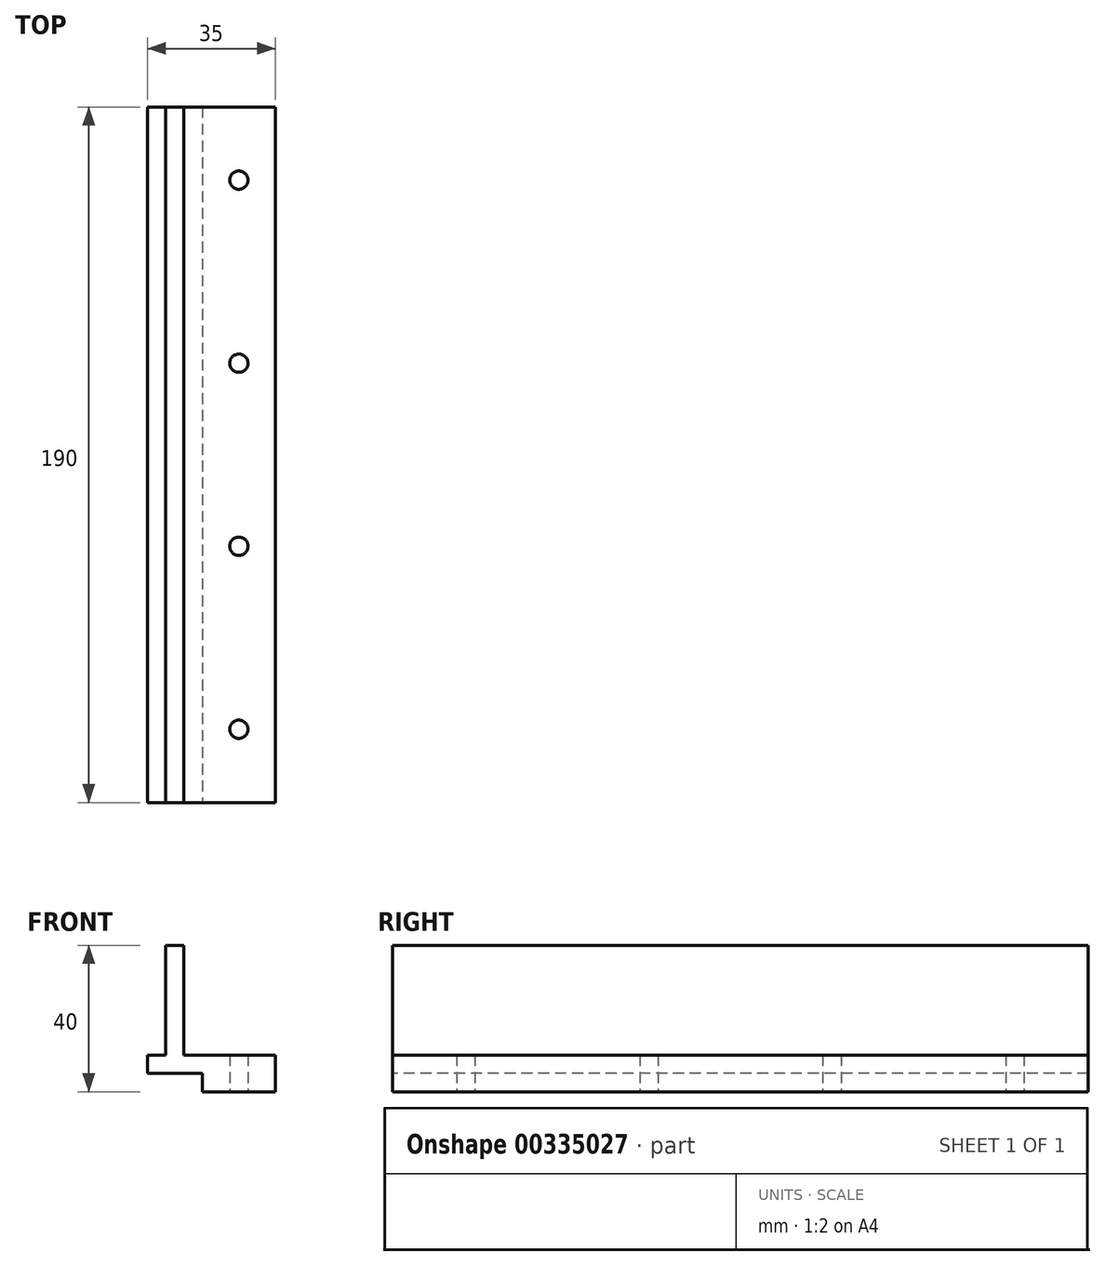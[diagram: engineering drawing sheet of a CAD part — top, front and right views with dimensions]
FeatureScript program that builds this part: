
annotation { "Feature Type Name" : "Feature", "Feature Type Description" : "" }
export const myFeature = defineFeature(function(context is Context, id is Id, definition is map)
    precondition{}
    {
        {
            var Q0;
            Q0=qCreatedBy(makeId("Top.planeOp"),FACE);
            var sketch = newSketch(context, id + "F0", { "sketchPlane" : qUnion([Q0])});
            skLineSegment(sketch, "E0", {"start": v(0, 35.83) * mm, "end": v(0, -48.01) * mm, "construction": true});
            skCircle(sketch, "E1", {"center": v(0, -28.01) * mm, "radius": 2.5 * mm});
            skCircle(sketch, "E2.0.1.0", {"center": v(0, 21.99) * mm, "radius": 2.5 * mm});
            skCircle(sketch, "E2.0.2.0", {"center": v(0, 71.99) * mm, "radius": 2.5 * mm});
            skCircle(sketch, "E2.0.3.0", {"center": v(0, 121.99) * mm, "radius": 2.5 * mm});
            skLineSegment(sketch, "E2.direction1", {"start": v(0, -28.01) * mm, "end": v(25, -28.01) * mm, "construction": true});
            skLineSegment(sketch, "E2.direction2", {"start": v(0, -28.01) * mm, "end": v(0, 21.99) * mm, "construction": true});
            skLineSegment(sketch, "E3.bottom", {"start": v(-10, 141.99) * mm, "end": v(10, 141.99) * mm});
            skLineSegment(sketch, "E3.top", {"start": v(-10, -48.01) * mm, "end": v(10, -48.01) * mm});
            skLineSegment(sketch, "E3.left", {"start": v(-10, 141.99) * mm, "end": v(-10, -48.01) * mm});
            skLineSegment(sketch, "E3.right", {"start": v(10, 141.99) * mm, "end": v(10, -48.01) * mm});
            skSolve(sketch);
        }
        {
            var Q0;
            Q0=makeQuery(id+"F0.imprint","IMPRINT",FACE,{"disambiguationData":[TD([[makeQuery(id+"F0.imprint","IMPRINT",EDGE,{"derivedFrom":sQuery(id+"F0.wireOp",EDGE,"E1")}),-1.0]])]});
            extrude(context, id + "F1", {"entities" : qUnion([Q0]), "depth" : 10 * mm});
        }
        {
            var Q0;
            Q0=makeQuery(id+"F1.opExtrude","SWEPT_FACE",FACE,{"disambiguationData":[OSD([sQuery(id+"F0.wireOp",EDGE,"E3.left")])]});
            var sketch = newSketch(context, id + "F2", { "sketchPlane" : qUnion([Q0])});
            skLineSegment(sketch, "E4.bottom", {"start": v(-141.99, 10) * mm, "end": v(48.01, 10) * mm});
            skLineSegment(sketch, "E4.top", {"start": v(-141.99, 5) * mm, "end": v(48.01, 5) * mm});
            skLineSegment(sketch, "E4.left", {"start": v(-141.99, 10) * mm, "end": v(-141.99, 5) * mm});
            skLineSegment(sketch, "E4.right", {"start": v(48.01, 10) * mm, "end": v(48.01, 5) * mm});
            skSolve(sketch);
        }
        {
            var Q0;
            Q0 = qSketchRegion(id + "F2", true);
            extrude(context, id + "F3", {"entities" : qUnion([Q0]), "operationType" : NewBodyOperationType.ADD, "depth" : 15 * mm});
        }
        {
            var Q0;
            Q0=makeQuery(id+"F3.boolean.opBoolean","MERGE",FACE,{"derivedFrom":[makeQuery(id+"F1.opExtrude","CAP_FACE",FACE,{"disambiguationData":[OSD([sQuery(id+"F0.wireOp",EDGE,"E1"),sQuery(id+"F0.wireOp",EDGE,"E2.0.1.0"),sQuery(id+"F0.wireOp",EDGE,"E2.0.2.0"),sQuery(id+"F0.wireOp",EDGE,"E2.0.3.0"),sQuery(id+"F0.wireOp",EDGE,"E3.bottom"),sQuery(id+"F0.wireOp",EDGE,"E3.top"),sQuery(id+"F0.wireOp",EDGE,"E3.left"),sQuery(id+"F0.wireOp",EDGE,"E3.right")])],"isStart":false}),makeQuery(id+"F3.opExtrude","SWEPT_FACE",FACE,{"disambiguationData":[OSD([sQuery(id+"F2.wireOp",EDGE,"E4.bottom")])]})]});
            var sketch = newSketch(context, id + "F4", { "sketchPlane" : qUnion([Q0])});
            skLineSegment(sketch, "E5.bottom", {"start": v(-15, 141.99) * mm, "end": v(-20, 141.99) * mm});
            skLineSegment(sketch, "E5.top", {"start": v(-15, -48.01) * mm, "end": v(-20, -48.01) * mm});
            skLineSegment(sketch, "E5.left", {"start": v(-15, 141.99) * mm, "end": v(-15, -48.01) * mm});
            skLineSegment(sketch, "E5.right", {"start": v(-20, 141.99) * mm, "end": v(-20, -48.01) * mm});
            skSolve(sketch);
        }
        {
            var Q0;
            Q0=makeQuery(id+"F4.imprint","IMPRINT",FACE,{"disambiguationData":[TD([[makeQuery(id+"F4.imprint","IMPRINT",EDGE,{"derivedFrom":sQuery(id+"F4.wireOp",EDGE,"E5.bottom")}),-1.0]])]});
            extrude(context, id + "F5", {"entities" : qUnion([Q0]), "operationType" : NewBodyOperationType.ADD, "depth" : 30 * mm});
        }
    });
